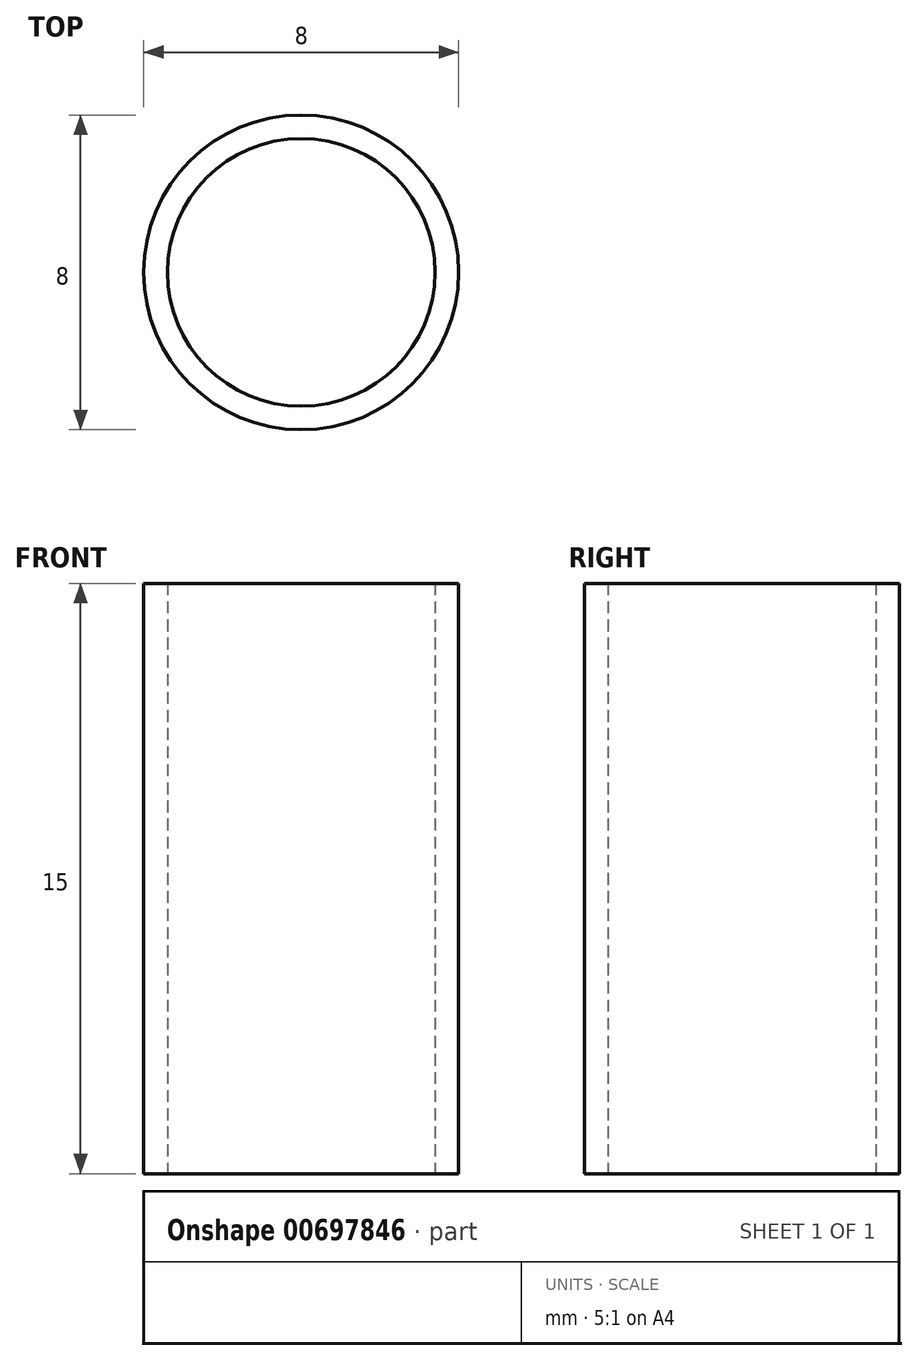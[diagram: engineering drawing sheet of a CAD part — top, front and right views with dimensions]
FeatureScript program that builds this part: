
annotation { "Feature Type Name" : "Feature", "Feature Type Description" : "" }
export const myFeature = defineFeature(function(context is Context, id is Id, definition is map)
    precondition{}
    {
        {
            var Q0;
            Q0=qCreatedBy(makeId("Top.planeOp"),FACE);
            var sketch = newSketch(context, id + "F0", { "sketchPlane" : qUnion([Q0])});
            skCircle(sketch, "E0", {"center": v(0, 0) * mm, "radius": 4 * mm});
            skCircle(sketch, "E1.0", {"center": v(0, 0) * mm, "radius": 3.4 * mm});
            skSolve(sketch);
        }
        {
            var Q0;
            Q0 = qSketchRegion(id + "F0", true);
            extrude(context, id + "F1", {"entities" : qUnion([Q0]), "depth" : 15 * mm, "offsetDistance" : 25 * mm});
        }
    });
